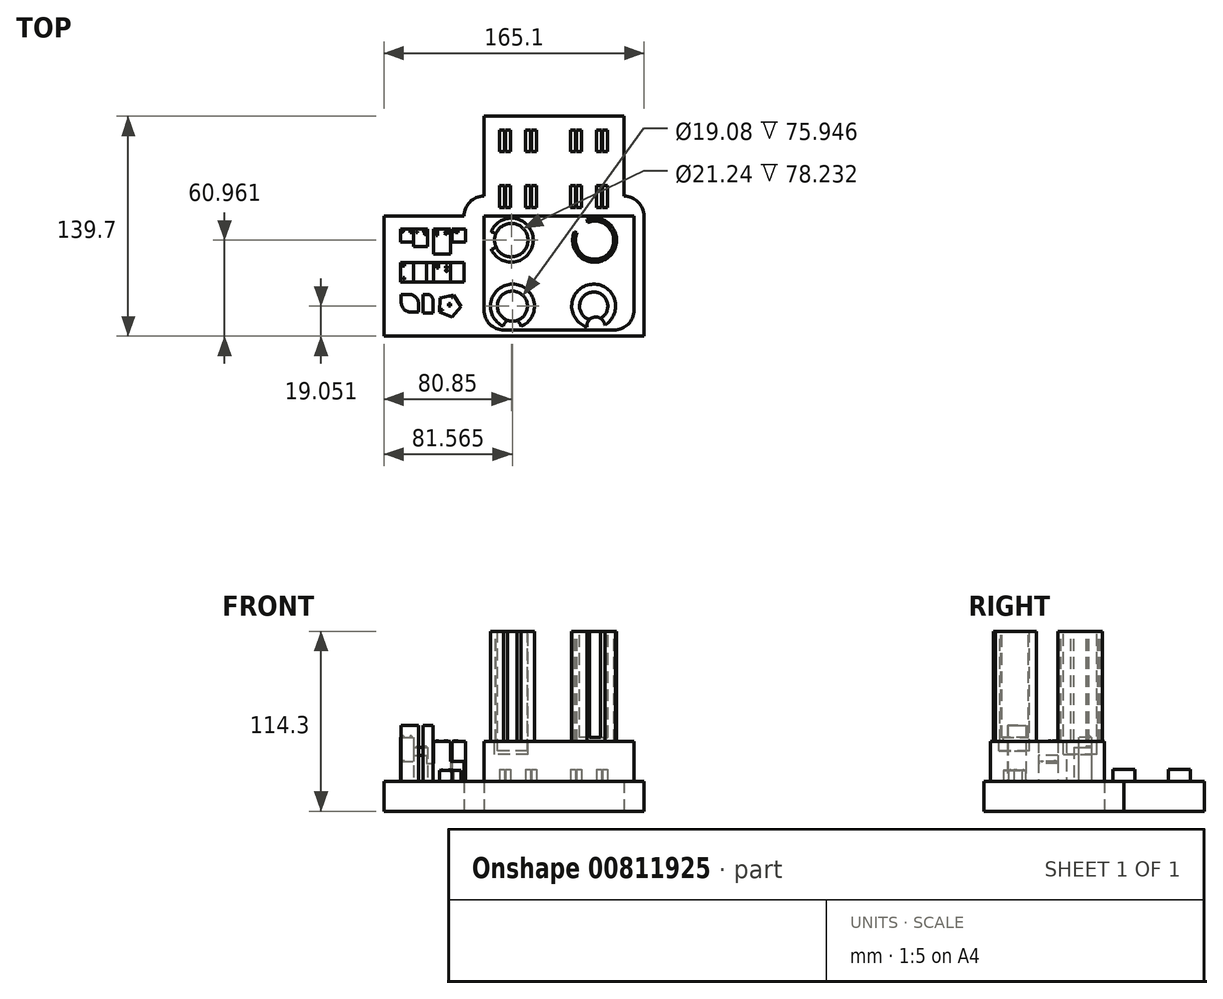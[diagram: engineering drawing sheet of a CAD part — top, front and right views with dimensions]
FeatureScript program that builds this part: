
annotation { "Feature Type Name" : "Feature", "Feature Type Description" : "" }
export const myFeature = defineFeature(function(context is Context, id is Id, definition is map)
    precondition{}
    {
        {
            var Q0;
            Q0=qCreatedBy(makeId("Top.planeOp"),FACE);
            var sketch = newSketch(context, id + "F0", { "sketchPlane" : qUnion([Q0])});
            skLineSegment(sketch, "E0.bottom", {"start": v(-36.01, 62.32) * mm, "end": v(52.89, 62.32) * mm});
            skLineSegment(sketch, "E0.top", {"start": v(-48.71, -26.58) * mm, "end": v(65.59, -26.58) * mm});
            skLineSegment(sketch, "E0.left", {"start": v(-48.71, 49.62) * mm, "end": v(-48.71, -26.58) * mm});
            skLineSegment(sketch, "E0.right", {"start": v(65.59, 49.62) * mm, "end": v(65.59, -26.58) * mm});
            skPoint(sketch, "E1.visualSharp", {"position": v(-48.71, 62.32) * mm});
            skArc(sketch, "E1.filletArc", {"start": v(-36.01, 62.32) * mm, "mid": v(-45, 58.6) * mm, "end": v(-48.71, 49.62) * mm});
            skPoint(sketch, "E2.visualSharp", {"position": v(65.59, 62.32) * mm});
            skArc(sketch, "E2.filletArc", {"start": v(65.59, 49.62) * mm, "mid": v(61.87, 58.6) * mm, "end": v(52.89, 62.32) * mm});
            skSolve(sketch);
        }
        {
            var Q0;
            Q0 = qSketchRegion(id + "F0", true);
            extrude(context, id + "F1", {"entities" : qUnion([Q0]), "depth" : 19.05 * mm, "offsetDistance" : 25.4 * mm});
        }
        {
            var Q0;
            Q0=makeQuery(id+"F1.opExtrude","CAP_FACE",FACE,{"disambiguationData":[OSD([sQuery(id+"F0.wireOp",EDGE,"E0.bottom"),sQuery(id+"F0.wireOp",EDGE,"E0.top"),sQuery(id+"F0.wireOp",EDGE,"E0.left"),sQuery(id+"F0.wireOp",EDGE,"E0.right"),sQuery(id+"F0.wireOp",EDGE,"E1.filletArc"),sQuery(id+"F0.wireOp",EDGE,"E2.filletArc")])],"isStart":false});
            var sketch = newSketch(context, id + "F2", { "sketchPlane" : qUnion([Q0])});
            skLineSegment(sketch, "E3.bottom", {"start": v(-36.01, 49.62) * mm, "end": v(59.24, 49.62) * mm});
            skLineSegment(sketch, "E3.top", {"start": v(-23.31, -22.77) * mm, "end": v(46.54, -22.77) * mm});
            skLineSegment(sketch, "E3.left", {"start": v(-36.01, 49.62) * mm, "end": v(-36.01, -10.07) * mm});
            skLineSegment(sketch, "E3.right", {"start": v(59.24, 49.62) * mm, "end": v(59.24, -10.07) * mm});
            skPoint(sketch, "E4.visualSharp", {"position": v(-36.01, -22.77) * mm});
            skArc(sketch, "E4.filletArc", {"start": v(-36.01, -10.07) * mm, "mid": v(-32.3, -19.05) * mm, "end": v(-23.31, -22.77) * mm});
            skPoint(sketch, "E5.visualSharp", {"position": v(59.24, -22.77) * mm});
            skArc(sketch, "E5.filletArc", {"start": v(46.54, -22.77) * mm, "mid": v(55.52, -19.05) * mm, "end": v(59.24, -10.07) * mm});
            skSolve(sketch);
        }
        {
            var Q0;
            Q0=makeQuery(id+"F2.imprint","IMPRINT",FACE,{"disambiguationData":[TD([[makeQuery(id+"F2.imprint","IMPRINT",EDGE,{"derivedFrom":sQuery(id+"F2.wireOp",EDGE,"E3.bottom")}),-1.0]])]});
            extrude(context, id + "F3", {"entities" : qUnion([Q0]), "operationType" : NewBodyOperationType.ADD, "depth" : 25.4 * mm, "offsetDistance" : 25.4 * mm});
        }
        {
            var Q0;
            Q0=makeQuery(id+"F3.opExtrude","CAP_FACE",FACE,{"disambiguationData":[OSD([sQuery(id+"F2.wireOp",EDGE,"E3.bottom"),sQuery(id+"F2.wireOp",EDGE,"E3.top"),sQuery(id+"F2.wireOp",EDGE,"E3.left"),sQuery(id+"F2.wireOp",EDGE,"E3.right"),sQuery(id+"F2.wireOp",EDGE,"E4.filletArc"),sQuery(id+"F2.wireOp",EDGE,"E5.filletArc")])],"isStart":false});
            var sketch = newSketch(context, id + "F4", { "sketchPlane" : qUnion([Q0])});
            skCircle(sketch, "E6", {"center": v(-18.66, 34.38) * mm, "radius": 13.97 * mm});
            skCircle(sketch, "E7", {"center": v(34.27, 34.38) * mm, "radius": 13.97 * mm});
            skCircle(sketch, "E8", {"center": v(-17.95, -7.53) * mm, "radius": 13.97 * mm});
            skCircle(sketch, "E9", {"center": v(33.66, -7.53) * mm, "radius": 13.97 * mm});
            skSolve(sketch);
        }
        {
            var Q0;
            Q0=makeQuery(id+"F4.imprint","IMPRINT",FACE,{"disambiguationData":[TD([[makeQuery(id+"F4.imprint","IMPRINT",EDGE,{"derivedFrom":sQuery(id+"F4.wireOp",EDGE,"E6")}),1.0]])]});
            var Q1;
            Q1=makeQuery(id+"F4.imprint","IMPRINT",FACE,{"disambiguationData":[TD([[makeQuery(id+"F4.imprint","IMPRINT",EDGE,{"derivedFrom":sQuery(id+"F4.wireOp",EDGE,"E8")}),1.0]])]});
            var Q2;
            Q2=makeQuery(id+"F4.imprint","IMPRINT",FACE,{"disambiguationData":[TD([[makeQuery(id+"F4.imprint","IMPRINT",EDGE,{"derivedFrom":sQuery(id+"F4.wireOp",EDGE,"E9")}),1.0]])]});
            var Q3;
            Q3=makeQuery(id+"F4.imprint","IMPRINT",FACE,{"disambiguationData":[TD([[makeQuery(id+"F4.imprint","IMPRINT",EDGE,{"derivedFrom":sQuery(id+"F4.wireOp",EDGE,"E7")}),1.0]])]});
            extrude(context, id + "F5", {"entities" : qUnion([Q0, Q1, Q2, Q3]), "operationType" : NewBodyOperationType.ADD, "depth" : 69.85 * mm, "offsetDistance" : 25.4 * mm});
        }
        {
            var Q0;
            Q0=makeQuery(id+"F5.opExtrude","CAP_FACE",FACE,{"disambiguationData":[OSD([sQuery(id+"F4.wireOp",EDGE,"E7")])],"isStart":false});
            var sketch = newSketch(context, id + "F6", { "sketchPlane" : qUnion([Q0])});
            skCircle(sketch, "E10", {"center": v(34.27, 34.38) * mm, "radius": 12.14 * mm});
            skCircle(sketch, "E11", {"center": v(24.23, 44.75) * mm, "radius": 5.72 * mm});
            skSolve(sketch);
        }
        {
            var Q0;
            Q0 = qSketchRegion(id + "F6", true);
            var Q1;
            Q1=makeQuery(id+"F6.imprint","IMPRINT",FACE,{"disambiguationData":[TD([[makeQuery(id+"F6.imprint","IMPRINT",EDGE,{"derivedFrom":sQuery(id+"F6.wireOp",EDGE,"E10")}),1.0]])]});
            extrude(context, id + "F7", {"entities" : qUnion([Q0, Q1]), "operationType" : NewBodyOperationType.REMOVE, "oppositeDirection" : true, "depth" : 69.85 * mm, "offsetDistance" : 25.4 * mm});
        }
        {
            var Q0;
            Q0=makeQuery(id+"F5.opExtrude","CAP_FACE",FACE,{"disambiguationData":[OSD([sQuery(id+"F4.wireOp",EDGE,"E9")])],"isStart":false});
            var sketch = newSketch(context, id + "F8", { "sketchPlane" : qUnion([Q0])});
            skCircle(sketch, "E12", {"center": v(33.66, -7.53) * mm, "radius": 8.97 * mm});
            skSolve(sketch);
        }
        {
            var Q0;
            Q0 = qSketchRegion(id + "F8", true);
            extrude(context, id + "F9", {"entities" : qUnion([Q0]), "operationType" : NewBodyOperationType.REMOVE, "oppositeDirection" : true, "depth" : 67.3 * mm, "offsetDistance" : 25.4 * mm});
        }
        {
            var Q0;
            Q0=makeQuery(id+"F5.opExtrude","CAP_FACE",FACE,{"disambiguationData":[OSD([sQuery(id+"F4.wireOp",EDGE,"E8")])],"isStart":false});
            var sketch = newSketch(context, id + "F10", { "sketchPlane" : qUnion([Q0])});
            skCircle(sketch, "E13", {"center": v(-17.95, -7.53) * mm, "radius": 9.54 * mm});
            skSolve(sketch);
        }
        {
            var Q0;
            Q0 = qSketchRegion(id + "F10", true);
            extrude(context, id + "F11", {"entities" : qUnion([Q0]), "operationType" : NewBodyOperationType.REMOVE, "oppositeDirection" : true, "depth" : 75.95 * mm, "offsetDistance" : 25.4 * mm});
        }
        {
            var Q0;
            Q0=makeQuery(id+"F5.opExtrude","CAP_FACE",FACE,{"disambiguationData":[OSD([sQuery(id+"F4.wireOp",EDGE,"E6")])],"isStart":false});
            var sketch = newSketch(context, id + "F12", { "sketchPlane" : qUnion([Q0])});
            skCircle(sketch, "E14", {"center": v(-18.66, 34.38) * mm, "radius": 10.62 * mm});
            skSolve(sketch);
        }
        {
            var Q0;
            Q0 = qSketchRegion(id + "F12", true);
            extrude(context, id + "F13", {"entities" : qUnion([Q0]), "operationType" : NewBodyOperationType.REMOVE, "oppositeDirection" : true, "depth" : 78.23 * mm, "offsetDistance" : 25.4 * mm});
        }
        {
            var Q0;
            Q0=makeQuery(id+"F1.opExtrude","SWEPT_FACE",FACE,{"disambiguationData":[OSD([sQuery(id+"F0.wireOp",EDGE,"E0.left")])]});
            var sketch = newSketch(context, id + "F14", { "sketchPlane" : qUnion([Q0])});
            skLineSegment(sketch, "E15.bottom", {"start": v(-49.62, 19.05) * mm, "end": v(26.58, 19.05) * mm});
            skLineSegment(sketch, "E15.top", {"start": v(-49.62, 0) * mm, "end": v(26.58, 0) * mm});
            skLineSegment(sketch, "E15.left", {"start": v(-49.62, 19.05) * mm, "end": v(-49.62, 0) * mm});
            skLineSegment(sketch, "E15.right", {"start": v(26.58, 19.05) * mm, "end": v(26.58, 0) * mm});
            skSolve(sketch);
        }
        {
            var Q0;
            Q0 = qSketchRegion(id + "F14", true);
            extrude(context, id + "F15", {"entities" : qUnion([Q0]), "operationType" : NewBodyOperationType.ADD, "depth" : 50.8 * mm, "offsetDistance" : 25.4 * mm});
        }
        {
            var Q0;
            Q0=makeQuery(id+"F15.boolean.opBoolean","MERGE",FACE,{"derivedFrom":[makeQuery(id+"F1.opExtrude","CAP_FACE",FACE,{"disambiguationData":[OSD([sQuery(id+"F0.wireOp",EDGE,"E0.bottom"),sQuery(id+"F0.wireOp",EDGE,"E0.top"),sQuery(id+"F0.wireOp",EDGE,"E0.left"),sQuery(id+"F0.wireOp",EDGE,"E0.right"),sQuery(id+"F0.wireOp",EDGE,"E1.filletArc"),sQuery(id+"F0.wireOp",EDGE,"E2.filletArc")])],"isStart":false}),makeQuery(id+"F15.opExtrude","SWEPT_FACE",FACE,{"disambiguationData":[OSD([sQuery(id+"F14.wireOp",EDGE,"E15.bottom")])]})]});
            var sketch = newSketch(context, id + "F16", { "sketchPlane" : qUnion([Q0])});
            skLineSegment(sketch, "E16", {"start": v(-92.22, 41.44) * mm, "end": v(-92.22, -15.77) * mm});
            skLineSegment(sketch, "E17", {"start": v(-92.22, 41.44) * mm, "end": v(-43.67, 41.44) * mm});
            skLineSegment(sketch, "E18", {"start": v(-43.67, 41.44) * mm, "end": v(-43.67, -15.77) * mm});
            skLineSegment(sketch, "E19", {"start": v(-43.67, -15.77) * mm, "end": v(-92.22, -15.77) * mm});
            skLineSegment(sketch, "E20", {"start": v(-88.85, 41.44) * mm, "end": v(-88.85, 33.25) * mm});
            skLineSegment(sketch, "E21", {"start": v(-88.85, 33.25) * mm, "end": v(-80.8, 33.25) * mm});
            skLineSegment(sketch, "E22", {"start": v(-80.8, 33.25) * mm, "end": v(-80.8, 41.44) * mm});
            skLineSegment(sketch, "E23", {"start": v(-80.8, 41.44) * mm, "end": v(-80.8, 41.44) * mm});
            skLineSegment(sketch, "E24", {"start": v(-80.8, 41.44) * mm, "end": v(-80.8, 30.47) * mm});
            skLineSegment(sketch, "E25", {"start": v(-80.8, 30.47) * mm, "end": v(-71.77, 30.47) * mm});
            skLineSegment(sketch, "E26", {"start": v(-71.77, 30.47) * mm, "end": v(-71.77, 41.44) * mm});
            skLineSegment(sketch, "E27", {"start": v(-71.77, 41.44) * mm, "end": v(-56.37, 41.44) * mm});
            skLineSegment(sketch, "E28", {"start": v(-56.37, 41.44) * mm, "end": v(-56.37, 33.3) * mm});
            skLineSegment(sketch, "E29", {"start": v(-56.37, 33.3) * mm, "end": v(-47.62, 33.3) * mm});
            skLineSegment(sketch, "E30", {"start": v(-47.62, 33.3) * mm, "end": v(-47.62, 41.44) * mm});
            skLineSegment(sketch, "E31.bottom", {"start": v(-57.16, 25.6) * mm, "end": v(-67.94, 25.6) * mm});
            skLineSegment(sketch, "E31.top", {"start": v(-57.16, 41.44) * mm, "end": v(-67.94, 41.44) * mm});
            skLineSegment(sketch, "E31.left", {"start": v(-57.16, 25.6) * mm, "end": v(-57.16, 41.44) * mm});
            skLineSegment(sketch, "E31.right", {"start": v(-67.94, 25.6) * mm, "end": v(-67.94, 41.44) * mm});
            skLineSegment(sketch, "E32.bottom", {"start": v(-88.85, 20.23) * mm, "end": v(-48.71, 20.23) * mm});
            skLineSegment(sketch, "E32.top", {"start": v(-88.85, 7.86) * mm, "end": v(-48.71, 7.86) * mm});
            skLineSegment(sketch, "E32.left", {"start": v(-88.85, 20.23) * mm, "end": v(-88.85, 7.86) * mm});
            skLineSegment(sketch, "E32.right", {"start": v(-48.71, 20.23) * mm, "end": v(-48.71, 7.86) * mm});
            skLineSegment(sketch, "E33", {"start": v(-80.8, 20.23) * mm, "end": v(-80.8, 7.86) * mm});
            skLineSegment(sketch, "E34", {"start": v(-72.54, 20.23) * mm, "end": v(-72.54, 7.86) * mm});
            skLineSegment(sketch, "E35", {"start": v(-67.94, 20.23) * mm, "end": v(-67.94, 7.86) * mm});
            skPoint(sketch, "E35.startSnap0", {"position": v(-67.94, 33.51) * mm});
            skPoint(sketch, "E35.endSnap0", {"position": v(-67.94, 33.51) * mm});
            skLineSegment(sketch, "E36", {"start": v(-57.38, 20.23) * mm, "end": v(-57.38, 7.86) * mm});
            skLineSegment(sketch, "E37.bottom", {"start": v(-82.27, -11.4) * mm, "end": v(-77.52, -11.4) * mm});
            skLineSegment(sketch, "E37.top", {"start": v(-88.62, 0) * mm, "end": v(-83.87, 0) * mm});
            skLineSegment(sketch, "E37.left", {"start": v(-88.62, -5.04) * mm, "end": v(-88.62, 0) * mm});
            skLineSegment(sketch, "E37.right", {"start": v(-77.52, -11.4) * mm, "end": v(-77.52, -6.35) * mm});
            skPoint(sketch, "E38.visualSharp", {"position": v(-77.52, 0) * mm});
            skArc(sketch, "E38.filletArc", {"start": v(-77.52, -6.35) * mm, "mid": v(-79.38, -1.86) * mm, "end": v(-83.87, 0) * mm});
            skPoint(sketch, "E39.visualSharp", {"position": v(-88.62, -11.4) * mm});
            skArc(sketch, "E39.filletArc", {"start": v(-88.62, -5.04) * mm, "mid": v(-86.76, -9.53) * mm, "end": v(-82.27, -11.4) * mm});
            skLineSegment(sketch, "E40.bottom", {"start": v(-68.39, -11.96) * mm, "end": v(-74.79, -11.96) * mm});
            skLineSegment(sketch, "E40.top", {"start": v(-72.2, 0) * mm, "end": v(-74.79, 0) * mm});
            skLineSegment(sketch, "E40.left", {"start": v(-68.39, -11.96) * mm, "end": v(-68.39, -3.8) * mm});
            skLineSegment(sketch, "E40.right", {"start": v(-74.79, -11.96) * mm, "end": v(-74.79, 0) * mm});
            skPoint(sketch, "E41.visualSharp", {"position": v(-68.39, 0) * mm});
            skArc(sketch, "E41.filletArc", {"start": v(-68.39, -3.8) * mm, "mid": v(-69.5, -1.12) * mm, "end": v(-72.2, 0) * mm});
            skLineSegment(sketch, "E42.0", {"start": v(-55.38, -0.32) * mm, "end": v(-50.72, -7.65) * mm});
            skLineSegment(sketch, "E42.1", {"start": v(-50.72, -7.65) * mm, "end": v(-56.26, -14.35) * mm});
            skLineSegment(sketch, "E42.2", {"start": v(-56.26, -14.35) * mm, "end": v(-64.34, -11.15) * mm});
            skLineSegment(sketch, "E42.3", {"start": v(-64.34, -11.15) * mm, "end": v(-63.8, -2.48) * mm});
            skLineSegment(sketch, "E42.4", {"start": v(-63.8, -2.48) * mm, "end": v(-55.38, -0.32) * mm});
            skPoint(sketch, "E42.0.midPoint", {"position": v(-53.05, -3.99) * mm});
            skSolve(sketch);
        }
        {
            var Q0;
            {var subQ0=sQuery(id+"F16.wireOp",EDGE,"E20");Q0=makeQuery(id+"F16.imprint","IMPRINT",FACE,{"disambiguationData":[TD([[makeQuery(id+"F16.imprint","IMPRINT",EDGE,{"derivedFrom":subQ0}),1.0]])]});}
            extrude(context, id + "F17", {"entities" : qUnion([Q0]), "operationType" : NewBodyOperationType.ADD, "depth" : 27.94 * mm, "offsetDistance" : 25.4 * mm});
        }
        {
            var Q0;
            {var subQ0=sQuery(id+"F16.wireOp",EDGE,"E25");Q0=makeQuery(id+"F16.imprint","IMPRINT",FACE,{"disambiguationData":[TD([[makeQuery(id+"F16.imprint","IMPRINT",EDGE,{"derivedFrom":subQ0}),1.0]])]});}
            extrude(context, id + "F18", {"entities" : qUnion([Q0]), "operationType" : NewBodyOperationType.ADD, "depth" : 21.59 * mm, "offsetDistance" : 25.4 * mm});
        }
        {
            var Q0;
            {var subQ0=sQuery(id+"F16.wireOp",EDGE,"E30");Q0=makeQuery(id+"F16.imprint","IMPRINT",FACE,{"disambiguationData":[TD([[makeQuery(id+"F16.imprint","IMPRINT",EDGE,{"derivedFrom":subQ0}),1.0]])]});}
            var Q1;
            Q1=makeQuery(id+"F16.imprint","IMPRINT",FACE,{"disambiguationData":[TD([[makeQuery(id+"F16.imprint","IMPRINT",EDGE,{"derivedFrom":sQuery(id+"F16.wireOp",EDGE,"E31.bottom")}),-1.0]])]});
            extrude(context, id + "F19", {"entities" : qUnion([Q0, Q1]), "operationType" : NewBodyOperationType.ADD, "depth" : 25.4 * mm, "offsetDistance" : 25.4 * mm});
        }
        {
            var Q0;
            {var subQ0=sQuery(id+"F16.wireOp",EDGE,"E32.left");Q0=makeQuery(id+"F16.imprint","IMPRINT",FACE,{"disambiguationData":[TD([[makeQuery(id+"F16.imprint","IMPRINT",EDGE,{"derivedFrom":subQ0}),1.0]])]});}
            extrude(context, id + "F20", {"entities" : qUnion([Q0]), "operationType" : NewBodyOperationType.ADD, "depth" : 12.7 * mm, "offsetDistance" : 25.4 * mm});
        }
        {
            var Q0;
            {var subQ0=sQuery(id+"F16.wireOp",EDGE,"E33");Q0=makeQuery(id+"F16.imprint","IMPRINT",FACE,{"disambiguationData":[TD([[makeQuery(id+"F16.imprint","IMPRINT",EDGE,{"derivedFrom":subQ0}),1.0]])]});}
            extrude(context, id + "F21", {"entities" : qUnion([Q0]), "operationType" : NewBodyOperationType.ADD, "depth" : 16.5 * mm, "offsetDistance" : 25.4 * mm});
        }
        {
            var Q0;
            {var subQ0=sQuery(id+"F16.wireOp",EDGE,"E34");Q0=makeQuery(id+"F16.imprint","IMPRINT",FACE,{"disambiguationData":[TD([[makeQuery(id+"F16.imprint","IMPRINT",EDGE,{"derivedFrom":subQ0}),1.0]])]});}
            extrude(context, id + "F22", {"entities" : qUnion([Q0]), "operationType" : NewBodyOperationType.ADD, "depth" : 11.43 * mm, "offsetDistance" : 25.4 * mm});
        }
        {
            var Q0;
            {var subQ0=sQuery(id+"F16.wireOp",EDGE,"E35");Q0=makeQuery(id+"F16.imprint","IMPRINT",FACE,{"disambiguationData":[TD([[makeQuery(id+"F16.imprint","IMPRINT",EDGE,{"derivedFrom":subQ0}),1.0]])]});}
            extrude(context, id + "F23", {"entities" : qUnion([Q0]), "operationType" : NewBodyOperationType.ADD, "depth" : 25.4 * mm, "offsetDistance" : 25.4 * mm});
        }
        {
            var Q0;
            {var subQ0=sQuery(id+"F16.wireOp",EDGE,"E32.right");Q0=makeQuery(id+"F16.imprint","IMPRINT",FACE,{"disambiguationData":[TD([[makeQuery(id+"F16.imprint","IMPRINT",EDGE,{"derivedFrom":subQ0}),-1.0]])]});}
            extrude(context, id + "F24", {"entities" : qUnion([Q0]), "operationType" : NewBodyOperationType.ADD, "depth" : 12.7 * mm, "offsetDistance" : 25.4 * mm});
        }
        {
            var Q0;
            Q0=makeQuery(id+"F16.imprint","IMPRINT",FACE,{"disambiguationData":[TD([[makeQuery(id+"F16.imprint","IMPRINT",EDGE,{"derivedFrom":sQuery(id+"F16.wireOp",EDGE,"E37.bottom")}),1.0]])]});
            var Q1;
            Q1=makeQuery(id+"F16.imprint","IMPRINT",FACE,{"disambiguationData":[TD([[makeQuery(id+"F16.imprint","IMPRINT",EDGE,{"derivedFrom":sQuery(id+"F16.wireOp",EDGE,"E40.bottom")}),-1.0]])]});
            extrude(context, id + "F25", {"entities" : qUnion([Q0, Q1]), "operationType" : NewBodyOperationType.ADD, "depth" : 35.56 * mm, "offsetDistance" : 25.4 * mm});
        }
        {
            var Q0;
            Q0=makeQuery(id+"F16.imprint","IMPRINT",FACE,{"disambiguationData":[TD([[makeQuery(id+"F16.imprint","IMPRINT",EDGE,{"derivedFrom":sQuery(id+"F16.wireOp",EDGE,"E42.0")}),-1.0]])]});
            extrude(context, id + "F26", {"entities" : qUnion([Q0]), "operationType" : NewBodyOperationType.ADD, "depth" : 6.86 * mm, "offsetDistance" : 25.4 * mm});
        }
        {
            var Q0;
            Q0=makeQuery(id+"F1.opExtrude","SWEPT_FACE",FACE,{"disambiguationData":[OSD([sQuery(id+"F0.wireOp",EDGE,"E0.bottom")])]});
            extrude(context, id + "F27", {"entities" : qUnion([Q0]), "operationType" : NewBodyOperationType.ADD, "depth" : 50.8 * mm, "offsetDistance" : 25.4 * mm});
        }
        {
            var Q0;
            {var subQ0=sQuery(id+"F0.wireOp",EDGE,"E0.bottom");Q0=makeQuery(id+"F27.boolean.opBoolean","MERGE",FACE,{"derivedFrom":[makeQuery(id+"F15.boolean.opBoolean","MERGE",FACE,{"derivedFrom":[makeQuery(id+"F1.opExtrude","CAP_FACE",FACE,{"disambiguationData":[OSD([subQ0,sQuery(id+"F0.wireOp",EDGE,"E0.top"),sQuery(id+"F0.wireOp",EDGE,"E0.left"),sQuery(id+"F0.wireOp",EDGE,"E0.right"),sQuery(id+"F0.wireOp",EDGE,"E1.filletArc"),sQuery(id+"F0.wireOp",EDGE,"E2.filletArc")])],"isStart":false}),makeQuery(id+"F15.opExtrude","SWEPT_FACE",FACE,{"disambiguationData":[OSD([sQuery(id+"F14.wireOp",EDGE,"E15.bottom")])]})]}),makeQuery(id+"F27.opExtrude","SWEPT_FACE",FACE,{"disambiguationData":[OSD([subQ0]),TDD([makeQuery(id+"F1.opExtrude","CAP_EDGE",EDGE,{"disambiguationData":[OSD([subQ0])],"isStart":false})])]})]});}
            var sketch = newSketch(context, id + "F28", { "sketchPlane" : qUnion([Q0])});
            skLineSegment(sketch, "E43.bottom", {"start": v(-26.28, 104.47) * mm, "end": v(42.59, 104.47) * mm});
            skLineSegment(sketch, "E43.top", {"start": v(-26.28, 90.51) * mm, "end": v(42.59, 90.51) * mm});
            skLineSegment(sketch, "E43.left", {"start": v(-30.1, 100.66) * mm, "end": v(-30.1, 94.32) * mm});
            skLineSegment(sketch, "E43.right", {"start": v(46.4, 100.66) * mm, "end": v(46.4, 94.32) * mm});
            skPoint(sketch, "E44.visualSharp", {"position": v(-30.1, 104.47) * mm});
            skArc(sketch, "E44.filletArc", {"start": v(-26.28, 104.47) * mm, "mid": v(-28.98, 103.35) * mm, "end": v(-30.1, 100.66) * mm});
            skPoint(sketch, "E45.visualSharp", {"position": v(-30.1, 90.51) * mm});
            skArc(sketch, "E45.filletArc", {"start": v(-30.1, 94.32) * mm, "mid": v(-28.98, 91.63) * mm, "end": v(-26.28, 90.51) * mm});
            skPoint(sketch, "E46.visualSharp", {"position": v(46.4, 90.51) * mm});
            skArc(sketch, "E46.filletArc", {"start": v(42.59, 90.51) * mm, "mid": v(45.28, 91.63) * mm, "end": v(46.4, 94.32) * mm});
            skPoint(sketch, "E47.visualSharp", {"position": v(46.4, 104.47) * mm});
            skArc(sketch, "E47.filletArc", {"start": v(46.4, 100.66) * mm, "mid": v(45.28, 103.35) * mm, "end": v(42.59, 104.47) * mm});
            skLineSegment(sketch, "E48", {"start": v(-26.28, 104.47) * mm, "end": v(-26.28, 90.51) * mm});
            skLineSegment(sketch, "E49", {"start": v(-23.1, 104.47) * mm, "end": v(-23.1, 90.51) * mm});
            skLineSegment(sketch, "E50", {"start": v(-22.34, 104.47) * mm, "end": v(-22.34, 90.51) * mm});
            skLineSegment(sketch, "E51", {"start": v(-19.16, 104.47) * mm, "end": v(-19.16, 90.51) * mm});
            skLineSegment(sketch, "E52", {"start": v(-9.74, 104.47) * mm, "end": v(-9.74, 90.51) * mm});
            skLineSegment(sketch, "E53", {"start": v(-6.57, 104.47) * mm, "end": v(-6.57, 90.51) * mm});
            skLineSegment(sketch, "E54", {"start": v(-5.8, 104.47) * mm, "end": v(-5.8, 90.51) * mm});
            skLineSegment(sketch, "E55", {"start": v(-2.63, 104.47) * mm, "end": v(-2.63, 90.51) * mm});
            skLineSegment(sketch, "E56", {"start": v(8.15, 104.47) * mm, "end": v(8.15, 90.51) * mm, "construction": true});
            skArc(sketch, "E57.MirrorCS", {"start": v(42.59, 104.47) * mm, "mid": v(45.28, 103.35) * mm, "end": v(46.4, 100.66) * mm});
            skLineSegment(sketch, "E58.MirrorCS", {"start": v(42.59, 104.47) * mm, "end": v(42.59, 90.51) * mm});
            skLineSegment(sketch, "E59.MirrorCS", {"start": v(18.93, 104.47) * mm, "end": v(18.93, 90.51) * mm});
            skLineSegment(sketch, "E60.MirrorCS", {"start": v(26.04, 104.47) * mm, "end": v(26.04, 90.51) * mm});
            skLineSegment(sketch, "E61.MirrorCS", {"start": v(35.46, 104.47) * mm, "end": v(35.46, 90.51) * mm});
            skArc(sketch, "E62.MirrorCS", {"start": v(46.4, 94.32) * mm, "mid": v(45.28, 91.63) * mm, "end": v(42.59, 90.51) * mm});
            skLineSegment(sketch, "E63.MirrorCS", {"start": v(38.64, 104.47) * mm, "end": v(38.64, 90.51) * mm});
            skLineSegment(sketch, "E64.MirrorCS", {"start": v(39.4, 104.47) * mm, "end": v(39.4, 90.51) * mm});
            skLineSegment(sketch, "E65.MirrorCS", {"start": v(22.87, 104.47) * mm, "end": v(22.87, 90.51) * mm});
            skLineSegment(sketch, "E66.MirrorCS", {"start": v(22.1, 104.47) * mm, "end": v(22.1, 90.51) * mm});
            skLineSegment(sketch, "E67", {"start": v(-36.01, 77.85) * mm, "end": v(52.89, 77.85) * mm, "construction": true});
            skArc(sketch, "E68.MirrorCS", {"start": v(46.4, 58.85) * mm, "mid": v(45.28, 56.16) * mm, "end": v(42.59, 55.04) * mm});
            skArc(sketch, "E69.MirrorCS", {"start": v(46.4, 65.18) * mm, "mid": v(45.28, 67.88) * mm, "end": v(42.59, 69) * mm});
            skArc(sketch, "E70.MirrorCS", {"start": v(42.59, 69) * mm, "mid": v(45.28, 67.88) * mm, "end": v(46.4, 65.18) * mm});
            skArc(sketch, "E71.MirrorCS", {"start": v(42.59, 55.04) * mm, "mid": v(45.28, 56.16) * mm, "end": v(46.4, 58.85) * mm});
            skArc(sketch, "E72.MirrorCS", {"start": v(-26.28, 55.04) * mm, "mid": v(-28.98, 56.16) * mm, "end": v(-30.1, 58.85) * mm});
            skPoint(sketch, "E73.MirrorP", {"position": v(46.4, 55.04) * mm});
            skLineSegment(sketch, "E74.MirrorCS", {"start": v(39.4, 55.04) * mm, "end": v(39.4, 69) * mm});
            skPoint(sketch, "E75.MirrorP", {"position": v(46.4, 69) * mm});
            skArc(sketch, "E76.MirrorCS", {"start": v(-30.1, 65.18) * mm, "mid": v(-28.98, 67.88) * mm, "end": v(-26.28, 69) * mm});
            skLineSegment(sketch, "E77.MirrorCS", {"start": v(46.4, 58.85) * mm, "end": v(46.4, 65.18) * mm});
            skLineSegment(sketch, "E78.MirrorCS", {"start": v(35.46, 55.04) * mm, "end": v(35.46, 69) * mm});
            skLineSegment(sketch, "E79.MirrorCS", {"start": v(42.59, 55.04) * mm, "end": v(42.59, 69) * mm});
            skLineSegment(sketch, "E80.MirrorCS", {"start": v(-26.28, 55.04) * mm, "end": v(-26.28, 69) * mm});
            skLineSegment(sketch, "E81.MirrorCS", {"start": v(-9.74, 55.04) * mm, "end": v(-9.74, 69) * mm});
            skPoint(sketch, "E82.MirrorP", {"position": v(-30.1, 69) * mm});
            skLineSegment(sketch, "E83.MirrorCS", {"start": v(8.15, 55.04) * mm, "end": v(8.15, 69) * mm, "construction": true});
            skLineSegment(sketch, "E84.MirrorCS", {"start": v(-26.28, 55.04) * mm, "end": v(42.59, 55.04) * mm});
            skLineSegment(sketch, "E85.MirrorCS", {"start": v(26.04, 55.04) * mm, "end": v(26.04, 69) * mm});
            skLineSegment(sketch, "E86.MirrorCS", {"start": v(22.1, 55.04) * mm, "end": v(22.1, 69) * mm});
            skLineSegment(sketch, "E87.MirrorCS", {"start": v(-23.1, 55.04) * mm, "end": v(-23.1, 69) * mm});
            skLineSegment(sketch, "E88.MirrorCS", {"start": v(-26.28, 69) * mm, "end": v(42.59, 69) * mm});
            skPoint(sketch, "E89.MirrorP", {"position": v(-30.1, 55.04) * mm});
            skLineSegment(sketch, "E90.MirrorCS", {"start": v(-30.1, 58.85) * mm, "end": v(-30.1, 65.18) * mm});
            skLineSegment(sketch, "E91.MirrorCS", {"start": v(-6.57, 55.04) * mm, "end": v(-6.57, 69) * mm});
            skLineSegment(sketch, "E92.MirrorCS", {"start": v(-22.34, 55.04) * mm, "end": v(-22.34, 69) * mm});
            skLineSegment(sketch, "E93.MirrorCS", {"start": v(22.87, 55.04) * mm, "end": v(22.87, 69) * mm});
            skLineSegment(sketch, "E94.MirrorCS", {"start": v(38.64, 55.04) * mm, "end": v(38.64, 69) * mm});
            skLineSegment(sketch, "E95.MirrorCS", {"start": v(18.93, 55.04) * mm, "end": v(18.93, 69) * mm});
            skLineSegment(sketch, "E96.MirrorCS", {"start": v(-5.8, 55.04) * mm, "end": v(-5.8, 69) * mm});
            skLineSegment(sketch, "E97.MirrorCS", {"start": v(-2.63, 55.04) * mm, "end": v(-2.63, 69) * mm});
            skLineSegment(sketch, "E98.MirrorCS", {"start": v(-19.16, 55.04) * mm, "end": v(-19.16, 69) * mm});
            skSolve(sketch);
        }
        {
            var Q0;
            {var subQ0=sQuery(id+"F28.wireOp",EDGE,"E48");Q0=makeQuery(id+"F28.imprint","IMPRINT",FACE,{"disambiguationData":[TD([[makeQuery(id+"F28.imprint","IMPRINT",EDGE,{"derivedFrom":subQ0}),1.0]])]});}
            var Q1;
            {var subQ0=sQuery(id+"F28.wireOp",EDGE,"E50");Q1=makeQuery(id+"F28.imprint","IMPRINT",FACE,{"disambiguationData":[TD([[makeQuery(id+"F28.imprint","IMPRINT",EDGE,{"derivedFrom":subQ0}),1.0]])]});}
            var Q2;
            {var subQ0=sQuery(id+"F28.wireOp",EDGE,"E52");Q2=makeQuery(id+"F28.imprint","IMPRINT",FACE,{"disambiguationData":[TD([[makeQuery(id+"F28.imprint","IMPRINT",EDGE,{"derivedFrom":subQ0}),1.0]])]});}
            var Q3;
            {var subQ0=sQuery(id+"F28.wireOp",EDGE,"E54");Q3=makeQuery(id+"F28.imprint","IMPRINT",FACE,{"disambiguationData":[TD([[makeQuery(id+"F28.imprint","IMPRINT",EDGE,{"derivedFrom":subQ0}),1.0]])]});}
            extrude(context, id + "F29", {"entities" : qUnion([Q0, Q1, Q2, Q3]), "operationType" : NewBodyOperationType.ADD, "depth" : 7.62 * mm, "offsetDistance" : 25.4 * mm});
        }
        {
            var Q0;
            {var subQ0=sQuery(id+"F28.wireOp",EDGE,"E59.MirrorCS");Q0=makeQuery(id+"F28.imprint","IMPRINT",FACE,{"disambiguationData":[TD([[makeQuery(id+"F28.imprint","IMPRINT",EDGE,{"derivedFrom":subQ0}),1.0]])]});}
            var Q1;
            {var subQ0=sQuery(id+"F28.wireOp",EDGE,"E60.MirrorCS");Q1=makeQuery(id+"F28.imprint","IMPRINT",FACE,{"disambiguationData":[TD([[makeQuery(id+"F28.imprint","IMPRINT",EDGE,{"derivedFrom":subQ0}),-1.0]])]});}
            var Q2;
            {var subQ0=sQuery(id+"F28.wireOp",EDGE,"E61.MirrorCS");Q2=makeQuery(id+"F28.imprint","IMPRINT",FACE,{"disambiguationData":[TD([[makeQuery(id+"F28.imprint","IMPRINT",EDGE,{"derivedFrom":subQ0}),1.0]])]});}
            var Q3;
            {var subQ0=sQuery(id+"F28.wireOp",EDGE,"E58.MirrorCS");Q3=makeQuery(id+"F28.imprint","IMPRINT",FACE,{"disambiguationData":[TD([[makeQuery(id+"F28.imprint","IMPRINT",EDGE,{"derivedFrom":subQ0}),-1.0]])]});}
            extrude(context, id + "F30", {"entities" : qUnion([Q0, Q1, Q2, Q3]), "operationType" : NewBodyOperationType.ADD, "depth" : 7.62 * mm, "offsetDistance" : 25.4 * mm});
        }
        {
            var Q0;
            {var subQ0=sQuery(id+"F6.wireOp",EDGE,"E11");var subQ1=sQuery(id+"F6.wireOp",EDGE,"E10");var subQ2=makeQuery(id+"F6.imprint","INTERSECT",VERTEX,{"disambiguationData":[OD(0.0)],"derivedFrom":[subQ1,subQ0]});Q0=makeQuery(id+"F6.imprint","IMPRINT",FACE,{"disambiguationData":[TD([[makeQuery(id+"F6.imprint","IMPRINT",EDGE,{"disambiguationData":[TD([[subQ2,-1.0]])],"derivedFrom":subQ1}),-1.0]])]});}
            extrude(context, id + "F31", {"entities" : qUnion([Q0]), "operationType" : NewBodyOperationType.REMOVE, "oppositeDirection" : true, "depth" : 25.4 * mm, "offsetDistance" : 25.4 * mm});
        }
        {
            var Q0;
            Q0=makeQuery(id+"F5.opExtrude","CAP_FACE",FACE,{"disambiguationData":[OSD([sQuery(id+"F4.wireOp",EDGE,"E6")])],"isStart":false});
            var sketch = newSketch(context, id + "F32", { "sketchPlane" : qUnion([Q0])});
            skCircle(sketch, "E99", {"center": v(-32.63, 34.15) * mm, "radius": 5.72 * mm});
            skSolve(sketch);
        }
        {
            var Q0;
            Q0 = qSketchRegion(id + "F32", true);
            extrude(context, id + "F33", {"entities" : qUnion([Q0]), "operationType" : NewBodyOperationType.REMOVE, "oppositeDirection" : true, "depth" : 69.85 * mm, "offsetDistance" : 25.4 * mm});
        }
        {
            var Q0;
            Q0=makeQuery(id+"F5.opExtrude","CAP_FACE",FACE,{"disambiguationData":[OSD([sQuery(id+"F4.wireOp",EDGE,"E8")])],"isStart":false});
            var sketch = newSketch(context, id + "F34", { "sketchPlane" : qUnion([Q0])});
            skCircle(sketch, "E100", {"center": v(-18.11, -21.5) * mm, "radius": 5.71 * mm});
            skSolve(sketch);
        }
        {
            var Q0;
            Q0 = qSketchRegion(id + "F34", true);
            extrude(context, id + "F35", {"entities" : qUnion([Q0]), "operationType" : NewBodyOperationType.REMOVE, "oppositeDirection" : true, "depth" : 69.85 * mm, "offsetDistance" : 25.4 * mm});
        }
        {
            var Q0;
            Q0=makeQuery(id+"F8.imprint","IMPRINT",FACE,{"disambiguationData":[TD([[makeQuery(id+"F8.imprint","IMPRINT",EDGE,{"derivedFrom":sQuery(id+"F8.wireOp",EDGE,"E12")}),-1.0]])]});
            var sketch = newSketch(context, id + "F36", { "sketchPlane" : qUnion([Q0])});
            skCircle(sketch, "E101", {"center": v(35.03, -20.1) * mm, "radius": 5.68 * mm});
            skSolve(sketch);
        }
        {
            var Q0;
            Q0 = qSketchRegion(id + "F36", true);
            extrude(context, id + "F37", {"entities" : qUnion([Q0]), "operationType" : NewBodyOperationType.REMOVE, "oppositeDirection" : true, "depth" : 69.85 * mm, "offsetDistance" : 25.4 * mm});
        }
        {
            var Q0;
            {var subQ0=sQuery(id+"F28.wireOp",EDGE,"E80.MirrorCS");Q0=makeQuery(id+"F28.imprint","IMPRINT",FACE,{"disambiguationData":[TD([[makeQuery(id+"F28.imprint","IMPRINT",EDGE,{"derivedFrom":subQ0}),-1.0]])]});}
            var Q1;
            {var subQ0=sQuery(id+"F28.wireOp",EDGE,"E92.MirrorCS");Q1=makeQuery(id+"F28.imprint","IMPRINT",FACE,{"disambiguationData":[TD([[makeQuery(id+"F28.imprint","IMPRINT",EDGE,{"derivedFrom":subQ0}),-1.0]])]});}
            var Q2;
            {var subQ0=sQuery(id+"F28.wireOp",EDGE,"E81.MirrorCS");Q2=makeQuery(id+"F28.imprint","IMPRINT",FACE,{"disambiguationData":[TD([[makeQuery(id+"F28.imprint","IMPRINT",EDGE,{"derivedFrom":subQ0}),-1.0]])]});}
            var Q3;
            {var subQ0=sQuery(id+"F28.wireOp",EDGE,"E96.MirrorCS");Q3=makeQuery(id+"F28.imprint","IMPRINT",FACE,{"disambiguationData":[TD([[makeQuery(id+"F28.imprint","IMPRINT",EDGE,{"derivedFrom":subQ0}),-1.0]])]});}
            var Q4;
            {var subQ0=sQuery(id+"F28.wireOp",EDGE,"E86.MirrorCS");Q4=makeQuery(id+"F28.imprint","IMPRINT",FACE,{"disambiguationData":[TD([[makeQuery(id+"F28.imprint","IMPRINT",EDGE,{"derivedFrom":subQ0}),1.0]])]});}
            var Q5;
            {var subQ0=sQuery(id+"F28.wireOp",EDGE,"E85.MirrorCS");Q5=makeQuery(id+"F28.imprint","IMPRINT",FACE,{"disambiguationData":[TD([[makeQuery(id+"F28.imprint","IMPRINT",EDGE,{"derivedFrom":subQ0}),1.0]])]});}
            var Q6;
            {var subQ0=sQuery(id+"F28.wireOp",EDGE,"E78.MirrorCS");Q6=makeQuery(id+"F28.imprint","IMPRINT",FACE,{"disambiguationData":[TD([[makeQuery(id+"F28.imprint","IMPRINT",EDGE,{"derivedFrom":subQ0}),-1.0]])]});}
            var Q7;
            {var subQ0=sQuery(id+"F28.wireOp",EDGE,"E74.MirrorCS");Q7=makeQuery(id+"F28.imprint","IMPRINT",FACE,{"disambiguationData":[TD([[makeQuery(id+"F28.imprint","IMPRINT",EDGE,{"derivedFrom":subQ0}),-1.0]])]});}
            extrude(context, id + "F38", {"entities" : qUnion([Q0, Q1, Q2, Q3, Q4, Q5, Q6, Q7]), "operationType" : NewBodyOperationType.ADD, "depth" : 7.62 * mm, "offsetDistance" : 25.4 * mm});
        }
        {
            var Q0;
            Q0=makeQuery(id+"F17.opExtrude","CAP_FACE",FACE,{"disambiguationData":[OSD([sQuery(id+"F16.wireOp",EDGE,"E17"),sQuery(id+"F16.wireOp",EDGE,"E20"),sQuery(id+"F16.wireOp",EDGE,"E21"),sQuery(id+"F16.wireOp",EDGE,"E24")])],"isStart":false});
            var sketch = newSketch(context, id + "F39", { "sketchPlane" : qUnion([Q0])});
            skLineSegment(sketch, "E102.bottom", {"start": v(-81.93, 39.26) * mm, "end": v(-82.87, 39.26) * mm});
            skLineSegment(sketch, "E102.top", {"start": v(-81.93, 40.33) * mm, "end": v(-82.87, 40.33) * mm});
            skLineSegment(sketch, "E102.left", {"start": v(-81.93, 39.26) * mm, "end": v(-81.93, 40.33) * mm});
            skLineSegment(sketch, "E102.right", {"start": v(-82.87, 39.26) * mm, "end": v(-82.87, 40.33) * mm});
            skCircle(sketch, "E103", {"center": v(-87.7, 40.13) * mm, "radius": 0.51 * mm});
            skSolve(sketch);
        }
        {
            var Q0;
            Q0=makeQuery(id+"F39.imprint","IMPRINT",FACE,{"disambiguationData":[TD([[makeQuery(id+"F39.imprint","IMPRINT",EDGE,{"derivedFrom":sQuery(id+"F39.wireOp",EDGE,"E103")}),1.0]])]});
            var Q1;
            Q1=makeQuery(id+"F39.imprint","IMPRINT",FACE,{"disambiguationData":[TD([[makeQuery(id+"F39.imprint","IMPRINT",EDGE,{"derivedFrom":sQuery(id+"F39.wireOp",EDGE,"E102.bottom")}),-1.0]])]});
            extrude(context, id + "F40", {"entities" : qUnion([Q0, Q1]), "operationType" : NewBodyOperationType.ADD, "depth" : 0.81 * mm, "offsetDistance" : 25.4 * mm});
        }
        {
            var Q0;
            Q0=makeQuery(id+"F18.opExtrude","CAP_FACE",FACE,{"disambiguationData":[OSD([sQuery(id+"F16.wireOp",EDGE,"E17"),sQuery(id+"F16.wireOp",EDGE,"E24"),sQuery(id+"F16.wireOp",EDGE,"E25"),sQuery(id+"F16.wireOp",EDGE,"E26")])],"isStart":false});
            var sketch = newSketch(context, id + "F41", { "sketchPlane" : qUnion([Q0])});
            skSolve(sketch);
        }
        {
            var Q0;
            {var subQ3=sQuery(id+"F16.wireOp",EDGE,"E17");Q0=makeQuery(id+"F41.imprint","IMPRINT",FACE,{"disambiguationData":[TD([[makeQuery(id+"F41.imprint","IMPRINT",EDGE,{"derivedFrom":makeQuery(id+"F18.opExtrude","CAP_EDGE",EDGE,{"disambiguationData":[OSD([subQ3])],"isStart":false})}),-1.0]])]});}
            var sketch = newSketch(context, id + "F42", { "sketchPlane" : qUnion([Q0])});
            skCircle(sketch, "E104", {"center": v(-73.46, 40.04) * mm, "radius": 0.89 * mm});
            skCircle(sketch, "E105", {"center": v(-73.37, 38.42) * mm, "radius": 0.52 * mm});
            skLineSegment(sketch, "E106.bottom", {"start": v(-79.3, 39.95) * mm, "end": v(-78.14, 39.95) * mm});
            skLineSegment(sketch, "E106.top", {"start": v(-79.3, 39.14) * mm, "end": v(-78.14, 39.14) * mm});
            skLineSegment(sketch, "E106.left", {"start": v(-79.3, 39.95) * mm, "end": v(-79.3, 39.14) * mm});
            skLineSegment(sketch, "E106.right", {"start": v(-78.14, 39.95) * mm, "end": v(-78.14, 39.14) * mm});
            skSolve(sketch);
        }
        {
            var Q0;
            Q0 = qSketchRegion(id + "F42", true);
            extrude(context, id + "F43", {"entities" : qUnion([Q0]), "operationType" : NewBodyOperationType.ADD, "depth" : 0.64 * mm, "offsetDistance" : 25.4 * mm});
        }
        {
            var Q0;
            Q0=makeQuery(id+"F19.opExtrude","CAP_FACE",FACE,{"disambiguationData":[OSD([sQuery(id+"F16.wireOp",EDGE,"E31.bottom"),sQuery(id+"F16.wireOp",EDGE,"E31.top"),sQuery(id+"F16.wireOp",EDGE,"E31.left"),sQuery(id+"F16.wireOp",EDGE,"E31.right")])],"isStart":false});
            var sketch = newSketch(context, id + "F44", { "sketchPlane" : qUnion([Q0])});
            skLineSegment(sketch, "E107.bottom", {"start": v(-66.58, 40.06) * mm, "end": v(-65.46, 40.06) * mm});
            skLineSegment(sketch, "E107.top", {"start": v(-66.58, 37.44) * mm, "end": v(-65.46, 37.44) * mm});
            skLineSegment(sketch, "E107.left", {"start": v(-66.58, 40.06) * mm, "end": v(-66.58, 37.44) * mm});
            skLineSegment(sketch, "E107.right", {"start": v(-65.46, 40.06) * mm, "end": v(-65.46, 37.44) * mm});
            skLineSegment(sketch, "E108.0", {"start": v(-59.47, 40.07) * mm, "end": v(-59.47, 37.8) * mm});
            skLineSegment(sketch, "E108.1", {"start": v(-59.47, 37.8) * mm, "end": v(-61.44, 38.94) * mm});
            skLineSegment(sketch, "E108.2", {"start": v(-61.44, 38.94) * mm, "end": v(-59.47, 40.07) * mm});
            skPoint(sketch, "E108.0.midPoint", {"position": v(-59.47, 38.94) * mm});
            skSolve(sketch);
        }
        {
            var Q0;
            Q0 = qSketchRegion(id + "F44", true);
            extrude(context, id + "F45", {"entities" : qUnion([Q0]), "operationType" : NewBodyOperationType.ADD, "depth" : 0.38 * mm, "offsetDistance" : 25.4 * mm});
        }
        {
            var Q0;
            Q0=makeQuery(id+"F19.opExtrude","CAP_FACE",FACE,{"disambiguationData":[OSD([sQuery(id+"F16.wireOp",EDGE,"E17"),sQuery(id+"F16.wireOp",EDGE,"E28"),sQuery(id+"F16.wireOp",EDGE,"E29"),sQuery(id+"F16.wireOp",EDGE,"E30")])],"isStart":false});
            var sketch = newSketch(context, id + "F46", { "sketchPlane" : qUnion([Q0])});
            skLineSegment(sketch, "E109.bottom", {"start": v(-55.3, 40.37) * mm, "end": v(-54.22, 40.37) * mm});
            skLineSegment(sketch, "E109.top", {"start": v(-55.3, 39.83) * mm, "end": v(-54.22, 39.83) * mm});
            skLineSegment(sketch, "E109.left", {"start": v(-55.3, 40.37) * mm, "end": v(-55.3, 39.83) * mm});
            skLineSegment(sketch, "E109.right", {"start": v(-54.22, 40.37) * mm, "end": v(-54.22, 39.83) * mm});
            skLineSegment(sketch, "E110.bottom", {"start": v(-54.22, 40.37) * mm, "end": v(-52.59, 40.37) * mm});
            skLineSegment(sketch, "E110.top", {"start": v(-54.22, 39.28) * mm, "end": v(-52.59, 39.28) * mm});
            skLineSegment(sketch, "E110.left", {"start": v(-54.22, 40.37) * mm, "end": v(-54.22, 39.28) * mm});
            skLineSegment(sketch, "E110.right", {"start": v(-52.59, 40.37) * mm, "end": v(-52.59, 39.28) * mm});
            skSolve(sketch);
        }
        {
            var Q0;
            Q0 = qSketchRegion(id + "F46", true);
            extrude(context, id + "F47", {"entities" : qUnion([Q0]), "operationType" : NewBodyOperationType.ADD, "depth" : 0.38 * mm, "offsetDistance" : 25.4 * mm});
        }
        {
            var Q0;
            Q0=makeQuery(id+"F20.opExtrude","CAP_FACE",FACE,{"disambiguationData":[OSD([sQuery(id+"F16.wireOp",EDGE,"E32.bottom"),sQuery(id+"F16.wireOp",EDGE,"E32.top"),sQuery(id+"F16.wireOp",EDGE,"E32.left"),sQuery(id+"F16.wireOp",EDGE,"E33")])],"isStart":false});
            var sketch = newSketch(context, id + "F48", { "sketchPlane" : qUnion([Q0])});
            skLineSegment(sketch, "E111.bottom", {"start": v(-87.63, 19.11) * mm, "end": v(-86.33, 19.11) * mm});
            skLineSegment(sketch, "E111.top", {"start": v(-87.63, 17.82) * mm, "end": v(-86.33, 17.82) * mm});
            skLineSegment(sketch, "E111.left", {"start": v(-87.63, 19.11) * mm, "end": v(-87.63, 17.82) * mm});
            skLineSegment(sketch, "E111.right", {"start": v(-86.33, 19.11) * mm, "end": v(-86.33, 17.82) * mm});
            skLineSegment(sketch, "E112.bottom", {"start": v(-86.33, 9.42) * mm, "end": v(-87.56, 9.42) * mm});
            skLineSegment(sketch, "E112.top", {"start": v(-86.33, 10.55) * mm, "end": v(-87.56, 10.55) * mm});
            skLineSegment(sketch, "E112.left", {"start": v(-86.33, 9.42) * mm, "end": v(-86.33, 10.55) * mm});
            skLineSegment(sketch, "E112.right", {"start": v(-87.56, 9.42) * mm, "end": v(-87.56, 10.55) * mm});
            skSolve(sketch);
        }
        {
            var Q0;
            Q0 = qSketchRegion(id + "F48", true);
            extrude(context, id + "F49", {"entities" : qUnion([Q0]), "operationType" : NewBodyOperationType.ADD, "depth" : 0.38 * mm, "offsetDistance" : 25.4 * mm});
        }
        {
            var Q0;
            Q0=makeQuery(id+"F23.opExtrude","CAP_FACE",FACE,{"disambiguationData":[OSD([sQuery(id+"F16.wireOp",EDGE,"E32.bottom"),sQuery(id+"F16.wireOp",EDGE,"E32.top"),sQuery(id+"F16.wireOp",EDGE,"E35"),sQuery(id+"F16.wireOp",EDGE,"E36")])],"isStart":false});
            var sketch = newSketch(context, id + "F50", { "sketchPlane" : qUnion([Q0])});
            skLineSegment(sketch, "E113.bottom", {"start": v(-66.1, 18.89) * mm, "end": v(-64.86, 18.89) * mm});
            skLineSegment(sketch, "E113.top", {"start": v(-66.1, 16.6) * mm, "end": v(-64.86, 16.6) * mm});
            skLineSegment(sketch, "E113.left", {"start": v(-66.1, 18.89) * mm, "end": v(-66.1, 16.6) * mm});
            skLineSegment(sketch, "E113.right", {"start": v(-64.86, 18.89) * mm, "end": v(-64.86, 16.6) * mm});
            skLineSegment(sketch, "E114.bottom", {"start": v(-59.26, 18.01) * mm, "end": v(-60.4, 18.01) * mm});
            skLineSegment(sketch, "E114.top", {"start": v(-59.26, 16.6) * mm, "end": v(-60.4, 16.6) * mm});
            skLineSegment(sketch, "E114.left", {"start": v(-59.26, 18.01) * mm, "end": v(-59.26, 16.6) * mm});
            skLineSegment(sketch, "E114.right", {"start": v(-60.4, 18.01) * mm, "end": v(-60.4, 16.6) * mm});
            skCircle(sketch, "E115", {"center": v(-59.77, 15.13) * mm, "radius": 0.63 * mm});
            skSolve(sketch);
        }
        {
            var Q0;
            Q0 = qSketchRegion(id + "F50", true);
            extrude(context, id + "F51", {"entities" : qUnion([Q0]), "operationType" : NewBodyOperationType.ADD, "depth" : 0.38 * mm, "offsetDistance" : 25.4 * mm});
        }
        {
            var Q0;
            Q0=makeQuery(id+"F26.opExtrude","CAP_FACE",FACE,{"disambiguationData":[OSD([sQuery(id+"F16.wireOp",EDGE,"E42.0"),sQuery(id+"F16.wireOp",EDGE,"E42.1"),sQuery(id+"F16.wireOp",EDGE,"E42.2"),sQuery(id+"F16.wireOp",EDGE,"E42.3"),sQuery(id+"F16.wireOp",EDGE,"E42.4")])],"isStart":false});
            var sketch = newSketch(context, id + "F52", { "sketchPlane" : qUnion([Q0])});
            skLineSegment(sketch, "E116.bottom", {"start": v(-58.63, -5.8) * mm, "end": v(-57.12, -5.8) * mm});
            skLineSegment(sketch, "E116.top", {"start": v(-58.63, -7.58) * mm, "end": v(-57.12, -7.58) * mm});
            skLineSegment(sketch, "E116.left", {"start": v(-58.63, -5.8) * mm, "end": v(-58.63, -7.58) * mm});
            skLineSegment(sketch, "E116.right", {"start": v(-57.12, -5.8) * mm, "end": v(-57.12, -7.58) * mm});
            skLineSegment(sketch, "E117.bottom", {"start": v(-62.94, -9.73) * mm, "end": v(-62.37, -9.73) * mm});
            skLineSegment(sketch, "E117.top", {"start": v(-62.94, -10.37) * mm, "end": v(-62.37, -10.37) * mm});
            skLineSegment(sketch, "E117.left", {"start": v(-62.94, -9.73) * mm, "end": v(-62.94, -10.37) * mm});
            skLineSegment(sketch, "E117.right", {"start": v(-62.37, -9.73) * mm, "end": v(-62.37, -10.37) * mm});
            skLineSegment(sketch, "E118.bottom", {"start": v(-56.54, -1.46) * mm, "end": v(-55.95, -1.46) * mm});
            skLineSegment(sketch, "E118.top", {"start": v(-56.54, -1.93) * mm, "end": v(-55.95, -1.93) * mm});
            skLineSegment(sketch, "E118.left", {"start": v(-56.54, -1.46) * mm, "end": v(-56.54, -1.93) * mm});
            skLineSegment(sketch, "E118.right", {"start": v(-55.95, -1.46) * mm, "end": v(-55.95, -1.93) * mm});
            skSolve(sketch);
        }
        {
            var Q0;
            Q0 = qSketchRegion(id + "F52", true);
            extrude(context, id + "F53", {"entities" : qUnion([Q0]), "operationType" : NewBodyOperationType.ADD, "depth" : 0.38 * mm, "offsetDistance" : 25.4 * mm});
        }
    });
